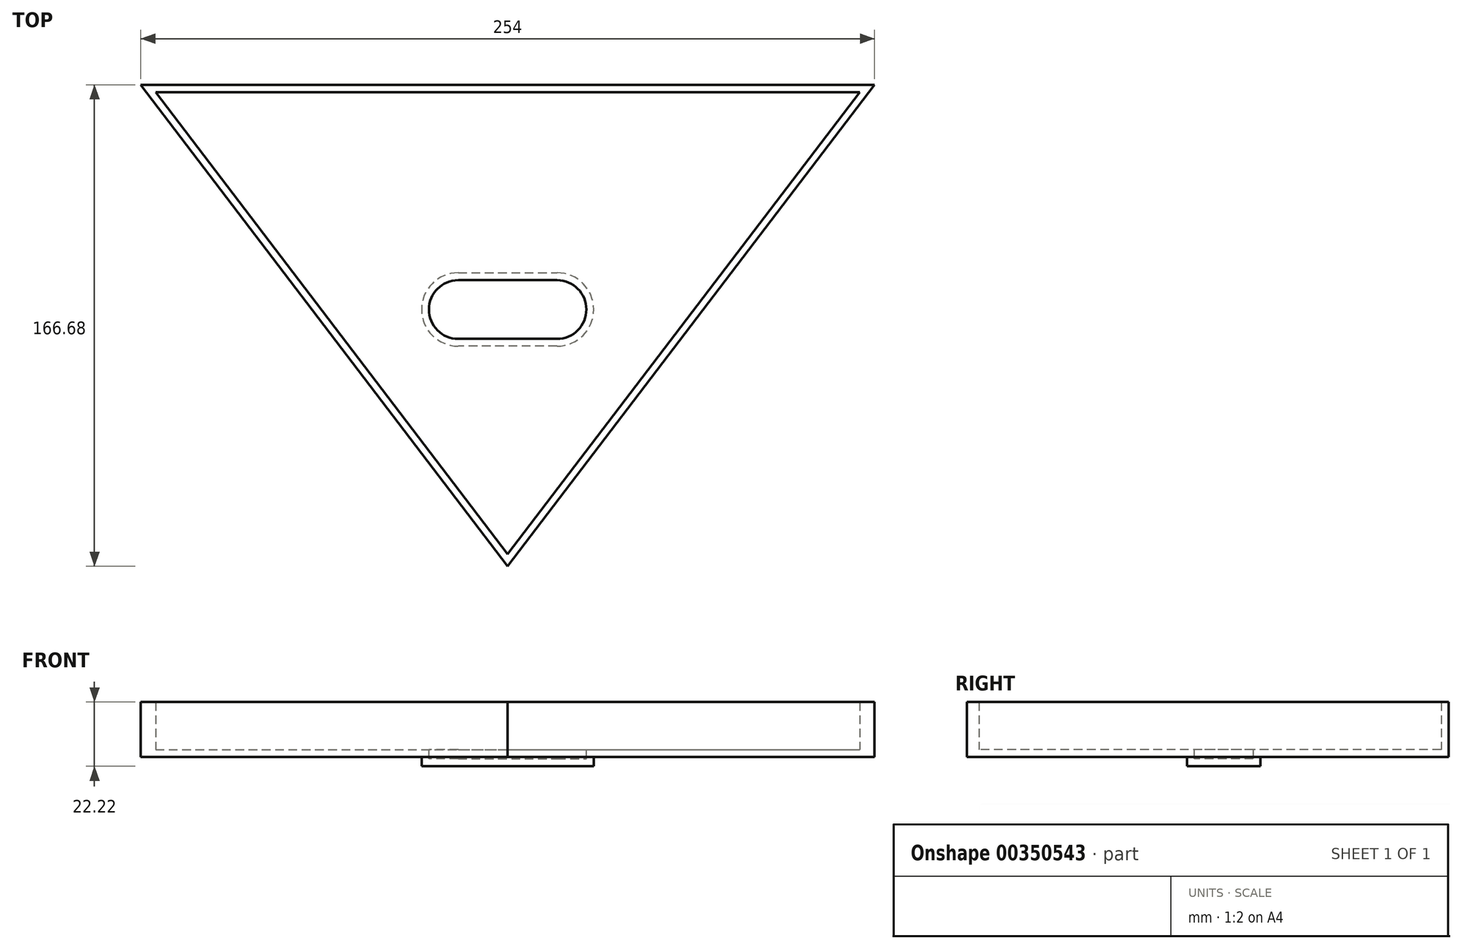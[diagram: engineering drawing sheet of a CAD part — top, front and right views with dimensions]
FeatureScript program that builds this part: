
annotation { "Feature Type Name" : "Feature", "Feature Type Description" : "" }
export const myFeature = defineFeature(function(context is Context, id is Id, definition is map)
    precondition{}
    {
        {
            var Q0;
            Q0=qCreatedBy(makeId("Top.planeOp"),FACE);
            var sketch = newSketch(context, id + "F0", { "sketchPlane" : qUnion([Q0])});
            skLineSegment(sketch, "E0", {"start": v(-127, 57.6) * mm, "end": v(127, 57.6) * mm});
            skLineSegment(sketch, "E1", {"start": v(-127, 57.6) * mm, "end": v(0, -109.08) * mm});
            skLineSegment(sketch, "E2", {"start": v(0, -109.08) * mm, "end": v(127, 57.6) * mm});
            skArc(sketch, "E3", {"start": v(-17.1, -7.48) * mm, "mid": v(-29.8, -20.18) * mm, "end": v(-17.1, -32.88) * mm});
            skArc(sketch, "E4.MirrorCS", {"start": v(17.1, -7.48) * mm, "mid": v(29.8, -20.18) * mm, "end": v(17.1, -32.88) * mm});
            skLineSegment(sketch, "E5", {"start": v(-17.1, -7.48) * mm, "end": v(17.1, -7.48) * mm});
            skLineSegment(sketch, "E6", {"start": v(17.1, -32.88) * mm, "end": v(-17.1, -32.88) * mm});
            skSolve(sketch);
        }
        {
            var Q0;
            Q0=makeQuery(id+"F0.imprint","IMPRINT",FACE,{"disambiguationData":[TD([[makeQuery(id+"F0.imprint","IMPRINT",EDGE,{"derivedFrom":sQuery(id+"F0.wireOp",EDGE,"E3")}),1.0]])]});
            extrude(context, id + "F1", {"entities" : qUnion([Q0]), "oppositeDirection" : true, "depth" : 3.17 * mm});
        }
        {
            var Q0;
            Q0 = qSketchRegion(id + "F0", true);
            var Q1;
            Q1=makeQuery(id+"F1.opExtrude","CAP_FACE",FACE,{"disambiguationData":[OSD([sQuery(id+"F0.wireOp",EDGE,"E3"),sQuery(id+"F0.wireOp",EDGE,"E4.MirrorCS"),sQuery(id+"F0.wireOp",EDGE,"E5"),sQuery(id+"F0.wireOp",EDGE,"E6")])],"isStart":true});
            extrude(context, id + "F2", {"entities" : qUnion([Q0, Q1]), "operationType" : NewBodyOperationType.ADD, "depth" : 19.05 * mm});
        }
        {
            var Q0;
            {var subQ0=sQuery(id+"F0.wireOp",EDGE,"E6");var subQ1=sQuery(id+"F0.wireOp",EDGE,"E5");var subQ2=sQuery(id+"F0.wireOp",EDGE,"E4.MirrorCS");var subQ3=sQuery(id+"F0.wireOp",EDGE,"E3");Q0=makeQuery(id+"F2.boolean.opBoolean","MERGE",FACE,{"derivedFrom":[makeQuery(id+"F2.opExtrude","CAP_FACE",FACE,{"disambiguationData":[OSD([sQuery(id+"F0.wireOp",EDGE,"E0"),sQuery(id+"F0.wireOp",EDGE,"E1"),sQuery(id+"F0.wireOp",EDGE,"E2"),subQ3,subQ2,subQ1,subQ0])],"isStart":false}),makeQuery(id+"F2.opExtrude","CAP_FACE",FACE,{"disambiguationData":[OSD([subQ3,subQ2,subQ1,subQ0])],"isStart":false})]});}
            shell(context, id + "F3", {"entities" : qUnion([Q0]), "thickness" : 2.54 * mm});
        }
    });
